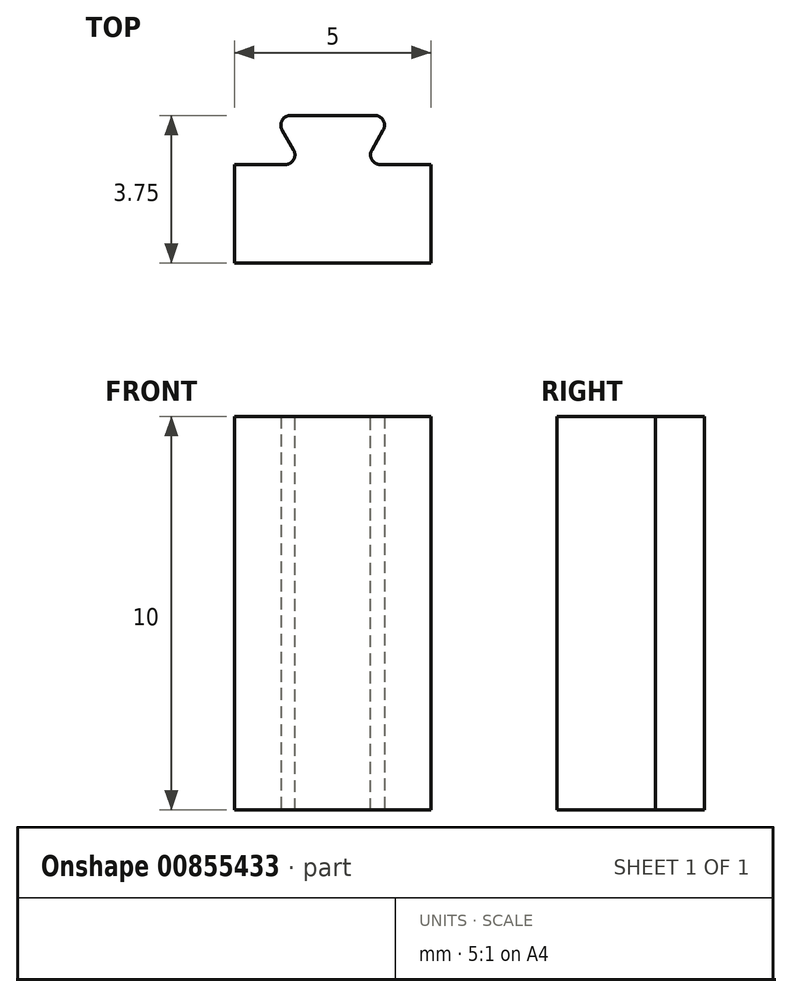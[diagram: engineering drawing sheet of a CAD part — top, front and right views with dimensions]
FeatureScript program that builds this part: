
annotation { "Feature Type Name" : "Feature", "Feature Type Description" : "" }
export const myFeature = defineFeature(function(context is Context, id is Id, definition is map)
    precondition{}
    {
        {
            var Q0;
            Q0=qCreatedBy(makeId("Top.planeOp"),FACE);
            var sketch = newSketch(context, id + "F0", { "sketchPlane" : qUnion([Q0])});
            skLineSegment(sketch, "E0.bottom", {"start": v(0, 0) * mm, "end": v(5, 0) * mm});
            skLineSegment(sketch, "E0.top", {"start": v(0, 2.5) * mm, "end": v(5, 2.5) * mm});
            skLineSegment(sketch, "E0.left", {"start": v(0, 0) * mm, "end": v(0, 2.5) * mm});
            skLineSegment(sketch, "E0.right", {"start": v(5, 0) * mm, "end": v(5, 2.5) * mm});
            skLineSegment(sketch, "E1", {"start": v(1.72, 2.5) * mm, "end": v(1, 3.75) * mm});
            skLineSegment(sketch, "E2", {"start": v(1, 3.75) * mm, "end": v(4, 3.75) * mm});
            skLineSegment(sketch, "E3", {"start": v(4, 3.75) * mm, "end": v(3.28, 2.5) * mm});
            skLineSegment(sketch, "E4", {"start": v(2.5, 0) * mm, "end": v(2.5, 3.75) * mm, "construction": true});
            skSolve(sketch);
        }
        {
            var Q0;
            Q0=makeQuery(id+"F0.imprint","IMPRINT",FACE,{"disambiguationData":[TD([[makeQuery(id+"F0.imprint","IMPRINT",EDGE,{"derivedFrom":sQuery(id+"F0.wireOp",EDGE,"E0.bottom")}),1.0]])]});
            var Q1;
            {var subQ0=sQuery(id+"F0.wireOp",EDGE,"E1");Q1=makeQuery(id+"F0.imprint","IMPRINT",FACE,{"disambiguationData":[TD([[makeQuery(id+"F0.imprint","IMPRINT",EDGE,{"derivedFrom":subQ0}),-1.0]])]});}
            extrude(context, id + "F1", {"entities" : qUnion([Q0, Q1]), "depth" : 10 * mm, "offsetDistance" : 25 * mm});
        }
        {
            var Q0;
            Q0=makeQuery(id+"F1.opExtrude","SWEPT_EDGE",EDGE,{"disambiguationData":[OSD([sQuery(id+"F0.wireOp",EDGE,"E0.top"),sQuery(id+"F0.wireOp",EDGE,"E1")])]});
            var Q1;
            Q1=makeQuery(id+"F1.opExtrude","SWEPT_EDGE",EDGE,{"disambiguationData":[OSD([sQuery(id+"F0.wireOp",EDGE,"E0.top"),sQuery(id+"F0.wireOp",EDGE,"E3")])]});
            var Q2;
            Q2=makeQuery(id+"F1.opExtrude","SWEPT_EDGE",EDGE,{"disambiguationData":[OSD([sQuery(id+"F0.wireOp",EDGE,"E2"),sQuery(id+"F0.wireOp",EDGE,"E3")])]});
            var Q3;
            Q3=makeQuery(id+"F1.opExtrude","SWEPT_EDGE",EDGE,{"disambiguationData":[OSD([sQuery(id+"F0.wireOp",EDGE,"E1"),sQuery(id+"F0.wireOp",EDGE,"E2")])]});
            fillet(context, id + "F2", {"entities" : qUnion([Q0, Q1, Q2, Q3]), "radius" : .25 * mm, "tangentPropagation" : true, "allowEdgeOverflow" : false});
        }
    });
